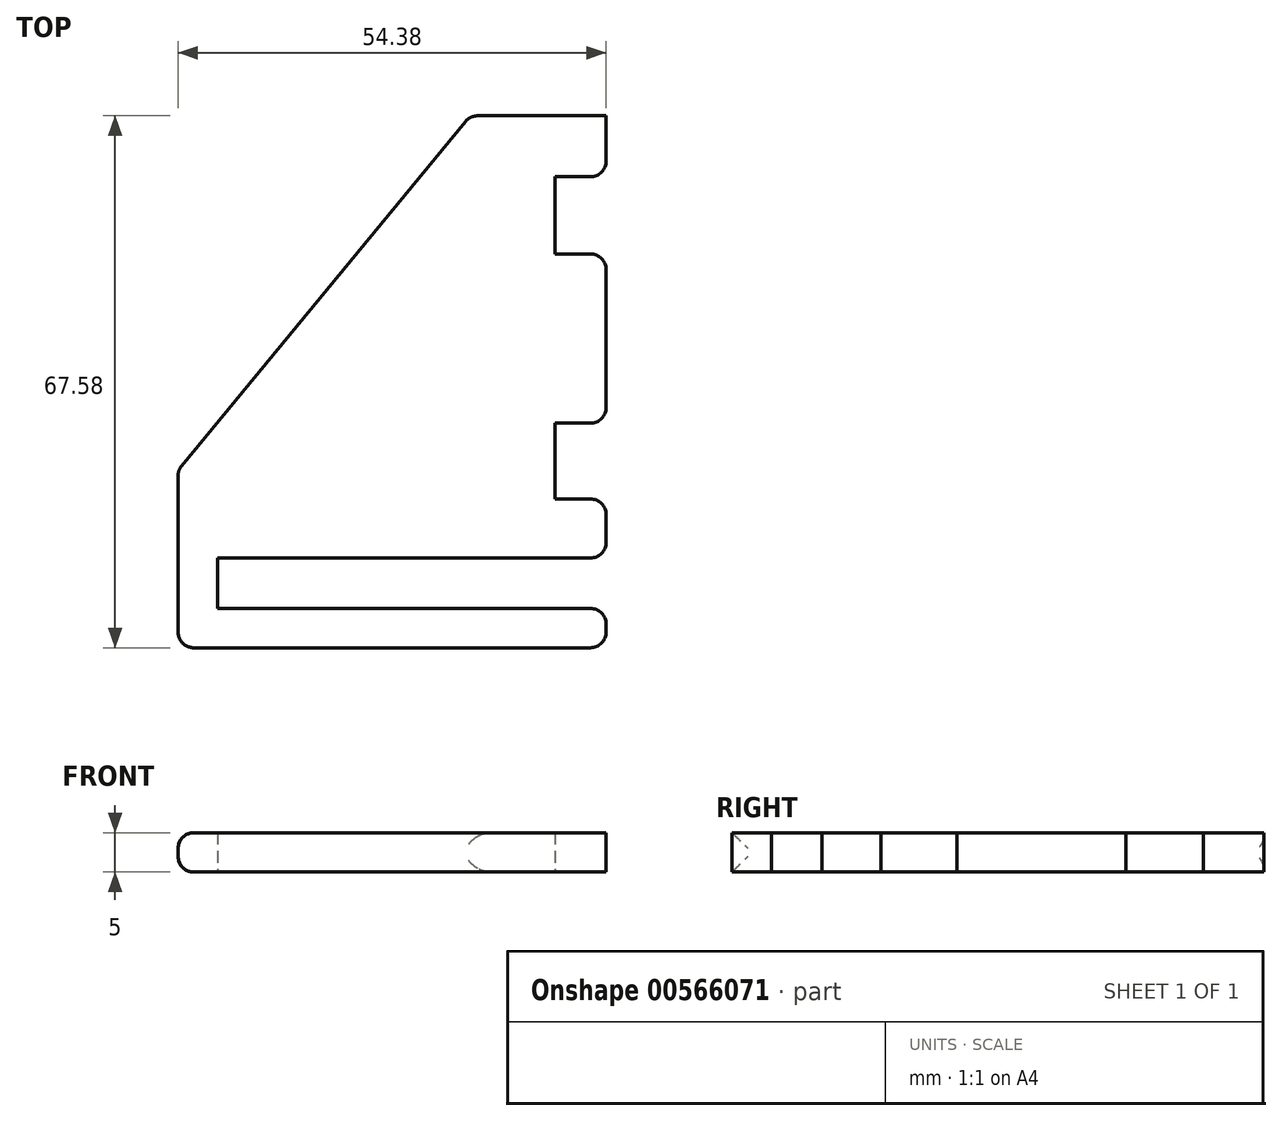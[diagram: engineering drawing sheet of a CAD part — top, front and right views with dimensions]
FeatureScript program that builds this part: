
annotation { "Feature Type Name" : "Feature", "Feature Type Description" : "" }
export const myFeature = defineFeature(function(context is Context, id is Id, definition is map)
    precondition{}
    {
        {
            var Q0;
            Q0=qCreatedBy(makeId("Top.planeOp"),FACE);
            var sketch = newSketch(context, id + "F0", { "sketchPlane" : qUnion([Q0])});
            skLineSegment(sketch, "E0", {"start": v(0, 7.5) * mm, "end": v(-6.5, 7.5) * mm});
            skLineSegment(sketch, "E1", {"start": v(0, 48.43) * mm, "end": v(-6.5, 48.43) * mm});
            skLineSegment(sketch, "E2", {"start": v(0, 38.63) * mm, "end": v(-6.5, 38.63) * mm});
            skLineSegment(sketch, "E3", {"start": v(-6.5, 17.13) * mm, "end": v(0, 17.13) * mm});
            skLineSegment(sketch, "E4", {"start": v(-49.38, 0) * mm, "end": v(-49.38, -6.4) * mm});
            skLineSegment(sketch, "E5", {"start": v(-49.38, -6.4) * mm, "end": v(0, -6.4) * mm});
            skLineSegment(sketch, "E6", {"start": v(0, -6.4) * mm, "end": v(0, -11.4) * mm});
            skLineSegment(sketch, "E7", {"start": v(0, -11.4) * mm, "end": v(-54.38, -11.4) * mm});
            skLineSegment(sketch, "E8", {"start": v(-54.38, -11.4) * mm, "end": v(-54.38, 11.15) * mm});
            skLineSegment(sketch, "E9", {"start": v(-6.5, 17.13) * mm, "end": v(-6.5, 7.5) * mm});
            skLineSegment(sketch, "E10", {"start": v(-6.5, 48.43) * mm, "end": v(-6.5, 38.63) * mm});
            skLineSegment(sketch, "E11.trimOffspring", {"start": v(0, 48.43) * mm, "end": v(0, 56.18) * mm});
            skLineSegment(sketch, "E12", {"start": v(-17.28, 56.18) * mm, "end": v(-54.38, 11.15) * mm});
            skLineSegment(sketch, "E13", {"start": v(0, 38.63) * mm, "end": v(0, 17.13) * mm});
            skLineSegment(sketch, "E14", {"start": v(0, 7.5) * mm, "end": v(0, 0) * mm});
            skLineSegment(sketch, "E15", {"start": v(-49.38, 0) * mm, "end": v(0, 0) * mm});
            skLineSegment(sketch, "E16", {"start": v(-17.28, 56.18) * mm, "end": v(0, 56.18) * mm});
            skSolve(sketch);
        }
        {
            var Q0;
            Q0 = qSketchRegion(id + "F0", true);
            extrude(context, id + "F1", {"entities" : qUnion([Q0]), "depth" : 5 * mm, "offsetDistance" : 25 * mm});
        }
        {
            var Q0;
            Q0=makeQuery(id+"F1.opExtrude","SWEPT_EDGE",EDGE,{"disambiguationData":[OSD([sQuery(id+"F0.wireOp",EDGE,"E1"),sQuery(id+"F0.wireOp",EDGE,"E11.trimOffspring")])]});
            var Q1;
            Q1=makeQuery(id+"F1.opExtrude","SWEPT_EDGE",EDGE,{"disambiguationData":[OSD([sQuery(id+"F0.wireOp",EDGE,"E2"),sQuery(id+"F0.wireOp",EDGE,"E13")])]});
            var Q2;
            Q2=makeQuery(id+"F1.opExtrude","SWEPT_EDGE",EDGE,{"disambiguationData":[OSD([sQuery(id+"F0.wireOp",EDGE,"E3"),sQuery(id+"F0.wireOp",EDGE,"E13")])]});
            var Q3;
            Q3=makeQuery(id+"F1.opExtrude","SWEPT_EDGE",EDGE,{"disambiguationData":[OSD([sQuery(id+"F0.wireOp",EDGE,"E0"),sQuery(id+"F0.wireOp",EDGE,"E14")])]});
            var Q4;
            Q4=makeQuery(id+"F1.opExtrude","SWEPT_EDGE",EDGE,{"disambiguationData":[OSD([sQuery(id+"F0.wireOp",EDGE,"E14"),sQuery(id+"F0.wireOp",EDGE,"E15")])]});
            var Q5;
            Q5=makeQuery(id+"F1.opExtrude","SWEPT_EDGE",EDGE,{"disambiguationData":[OSD([sQuery(id+"F0.wireOp",EDGE,"E5"),sQuery(id+"F0.wireOp",EDGE,"E6")])]});
            var Q6;
            Q6=makeQuery(id+"F1.opExtrude","SWEPT_EDGE",EDGE,{"disambiguationData":[OSD([sQuery(id+"F0.wireOp",EDGE,"E6"),sQuery(id+"F0.wireOp",EDGE,"E7")])]});
            var Q7;
            Q7=makeQuery(id+"F1.opExtrude","SWEPT_EDGE",EDGE,{"disambiguationData":[OSD([sQuery(id+"F0.wireOp",EDGE,"E12"),sQuery(id+"F0.wireOp",EDGE,"E16")])]});
            var Q8;
            Q8=makeQuery(id+"F1.opExtrude","SWEPT_EDGE",EDGE,{"disambiguationData":[OSD([sQuery(id+"F0.wireOp",EDGE,"E8"),sQuery(id+"F0.wireOp",EDGE,"E12")])]});
            var Q9;
            Q9=makeQuery(id+"F1.opExtrude","SWEPT_EDGE",EDGE,{"disambiguationData":[OSD([sQuery(id+"F0.wireOp",EDGE,"E7"),sQuery(id+"F0.wireOp",EDGE,"E8")])]});
            var Q10;
            Q10=makeQuery(id+"F1.opExtrude","CAP_EDGE",EDGE,{"disambiguationData":[OSD([sQuery(id+"F0.wireOp",EDGE,"E8")])],"isStart":true});
            var Q11;
            Q11=makeQuery(id+"F1.opExtrude","CAP_EDGE",EDGE,{"disambiguationData":[OSD([sQuery(id+"F0.wireOp",EDGE,"E8")])],"isStart":false});
            var Q12;
            Q12=makeQuery(id+"F1.opExtrude","CAP_EDGE",EDGE,{"disambiguationData":[OSD([sQuery(id+"F0.wireOp",EDGE,"E12")])],"isStart":true});
            var Q13;
            Q13=makeQuery(id+"F1.opExtrude","CAP_EDGE",EDGE,{"disambiguationData":[OSD([sQuery(id+"F0.wireOp",EDGE,"E12")])],"isStart":false});
            fillet(context, id + "F2", {"entities" : qUnion([Q0, Q1, Q2, Q3, Q4, Q5, Q6, Q7, Q8, Q9, Q10, Q11, Q12, Q13]), "radius" : 2 * mm, "tangentPropagation" : true, "allowEdgeOverflow" : false});
        }
    });
